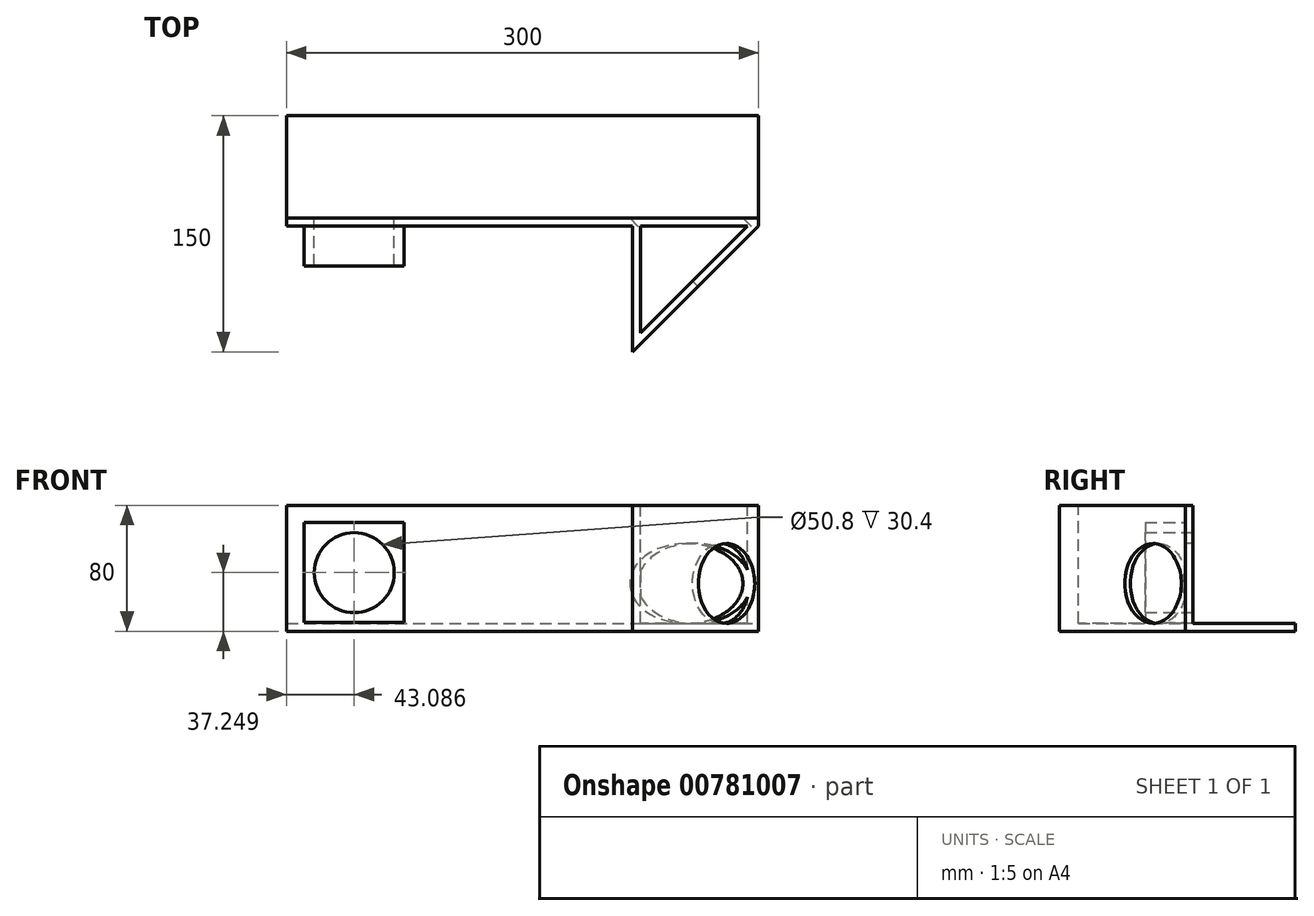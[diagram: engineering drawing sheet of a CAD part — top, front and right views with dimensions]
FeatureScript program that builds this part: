
annotation { "Feature Type Name" : "Feature", "Feature Type Description" : "" }
export const myFeature = defineFeature(function(context is Context, id is Id, definition is map)
    precondition{}
    {
        {
            var Q0;
            Q0=qCreatedBy(makeId("Top.planeOp"),FACE);
            var sketch = newSketch(context, id + "F0", { "sketchPlane" : qUnion([Q0])});
            skLineSegment(sketch, "E0.bottom", {"start": v(-205.2, 70) * mm, "end": v(94.8, 70) * mm});
            skLineSegment(sketch, "E0.top", {"start": v(-205.2, 0) * mm, "end": v(94.8, 0) * mm});
            skLineSegment(sketch, "E0.left", {"start": v(-205.2, 70) * mm, "end": v(-205.2, 0) * mm});
            skLineSegment(sketch, "E0.right", {"start": v(94.8, 70) * mm, "end": v(94.8, 0) * mm});
            skLineSegment(sketch, "E1", {"start": v(94.8, 0) * mm, "end": v(14.8, -80) * mm});
            skLineSegment(sketch, "E2", {"start": v(14.8, -80) * mm, "end": v(14.8, 0) * mm});
            skSolve(sketch);
        }
        {
            var Q0;
            Q0=makeQuery(id+"F0.imprint","IMPRINT",FACE,{"disambiguationData":[TD([[makeQuery(id+"F0.imprint","IMPRINT",EDGE,{"derivedFrom":sQuery(id+"F0.wireOp",EDGE,"E0.bottom")}),-1.0]])]});
            var Q1;
            {var subQ0=sQuery(id+"F0.wireOp",EDGE,"E1");Q1=makeQuery(id+"F0.imprint","IMPRINT",FACE,{"disambiguationData":[TD([[makeQuery(id+"F0.imprint","IMPRINT",EDGE,{"derivedFrom":subQ0}),-1.0]])]});}
            extrude(context, id + "F1", {"entities" : qUnion([Q0, Q1]), "depth" : 80 * mm, "offsetDistance" : 25.4 * mm});
        }
        {
            var Q0;
            Q0=makeQuery(id+"F1.opExtrude","CAP_FACE",FACE,{"disambiguationData":[OSD([sQuery(id+"F0.wireOp",EDGE,"E0.bottom"),sQuery(id+"F0.wireOp",EDGE,"E0.top"),sQuery(id+"F0.wireOp",EDGE,"E0.left"),sQuery(id+"F0.wireOp",EDGE,"E0.right"),sQuery(id+"F0.wireOp",EDGE,"E1"),sQuery(id+"F0.wireOp",EDGE,"E2")])],"isStart":false});
            var sketch = newSketch(context, id + "F2", { "sketchPlane" : qUnion([Q0])});
            skLineSegment(sketch, "E3", {"start": v(19.8, 0) * mm, "end": v(87.73, 0) * mm});
            skLineSegment(sketch, "E4", {"start": v(87.73, 0) * mm, "end": v(19.8, -67.93) * mm});
            skLineSegment(sketch, "E5", {"start": v(19.8, -67.93) * mm, "end": v(19.8, 0) * mm});
            skSolve(sketch);
        }
        {
            var Q0;
            Q0=makeQuery(id+"F2.imprint","IMPRINT",FACE,{"disambiguationData":[TD([[makeQuery(id+"F2.imprint","IMPRINT",EDGE,{"derivedFrom":sQuery(id+"F2.wireOp",EDGE,"E3")}),-1.0]])]});
            extrude(context, id + "F3", {"entities" : qUnion([Q0]), "operationType" : NewBodyOperationType.REMOVE, "oppositeDirection" : true, "depth" : 75 * mm, "offsetDistance" : 25.4 * mm});
        }
        {
            var Q0;
            Q0=makeQuery(id+"F1.opExtrude","SWEPT_FACE",FACE,{"disambiguationData":[OSD([sQuery(id+"F0.wireOp",EDGE,"E1")])]});
            var sketch = newSketch(context, id + "F4", { "sketchPlane" : qUnion([Q0])});
            skCircle(sketch, "E6", {"center": v(38.09, 30.4) * mm, "radius": 25.4 * mm});
            skSolve(sketch);
        }
        {
            var Q0;
            Q0=makeQuery(id+"F4.imprint","IMPRINT",FACE,{"disambiguationData":[TD([[makeQuery(id+"F4.imprint","IMPRINT",EDGE,{"derivedFrom":sQuery(id+"F4.wireOp",EDGE,"E6")}),1.0]])]});
            extrude(context, id + "F5", {"entities" : qUnion([Q0]), "operationType" : NewBodyOperationType.REMOVE, "oppositeDirection" : true, "depth" : 76.2 * mm, "offsetDistance" : 25.4 * mm});
        }
        {
            var Q0;
            Q0=makeQuery(id+"F1.opExtrude","SWEPT_FACE",FACE,{"disambiguationData":[OSD([sQuery(id+"F0.wireOp",EDGE,"E0.right")])]});
            var sketch = newSketch(context, id + "F6", { "sketchPlane" : qUnion([Q0])});
            skLineSegment(sketch, "E7", {"start": v(5, 80) * mm, "end": v(5, 5) * mm});
            skLineSegment(sketch, "E8", {"start": v(5, 5) * mm, "end": v(70, 5) * mm});
            skSolve(sketch);
        }
        {
            var Q0;
            Q0 = qSketchRegion(id + "F6", true);
            var Q1;
            {var subQ0=sQuery(id+"F6.wireOp",EDGE,"E7");Q1=makeQuery(id+"F6.imprint","IMPRINT",FACE,{"disambiguationData":[TD([[makeQuery(id+"F6.imprint","IMPRINT",EDGE,{"derivedFrom":subQ0}),1.0]])]});}
            extrude(context, id + "F7", {"entities" : qUnion([Q0, Q1]), "operationType" : NewBodyOperationType.REMOVE, "endBound" : BoundingType.THROUGH_ALL, "oppositeDirection" : true, "depth" : 25.4 * mm, "offsetDistance" : 25.4 * mm});
        }
        {
            var Q0;
            Q0=makeQuery(id+"F1.opExtrude","SWEPT_FACE",FACE,{"disambiguationData":[OSD([sQuery(id+"F0.wireOp",EDGE,"E0.top")])]});
            var sketch = newSketch(context, id + "F8", { "sketchPlane" : qUnion([Q0])});
            skLineSegment(sketch, "E9.bottom", {"start": v(-193.86, 69) * mm, "end": v(-130.36, 69) * mm});
            skLineSegment(sketch, "E9.top", {"start": v(-193.86, 5.5) * mm, "end": v(-130.36, 5.5) * mm});
            skLineSegment(sketch, "E9.left", {"start": v(-193.86, 69) * mm, "end": v(-193.86, 5.5) * mm});
            skLineSegment(sketch, "E9.right", {"start": v(-130.36, 69) * mm, "end": v(-130.36, 5.5) * mm});
            skCircle(sketch, "E10", {"center": v(-162.11, 37.25) * mm, "radius": 25.4 * mm});
            skPoint(sketch, "E11", {"position": v(-162.11, 69) * mm});
            skPoint(sketch, "E12", {"position": v(-130.36, 37.25) * mm});
            skPoint(sketch, "E13", {"position": v(-162.11, 5.5) * mm});
            skPoint(sketch, "E14", {"position": v(-193.86, 37.25) * mm});
            skSolve(sketch);
        }
        {
            var Q0;
            Q0=makeQuery(id+"F8.imprint","IMPRINT",FACE,{"disambiguationData":[TD([[makeQuery(id+"F8.imprint","IMPRINT",EDGE,{"derivedFrom":sQuery(id+"F8.wireOp",EDGE,"E9.bottom")}),-1.0]])]});
            extrude(context, id + "F9", {"entities" : qUnion([Q0]), "operationType" : NewBodyOperationType.ADD, "depth" : 25.4 * mm, "offsetDistance" : 25.4 * mm});
        }
        {
            var Q0;
            Q0=makeQuery(id+"F9.boolean.opBoolean","SPLIT",FACE,{"disambiguationData":[TD([makeQuery(id+"F9.opExtrude","SWEPT_FACE",FACE,{"disambiguationData":[OSD([sQuery(id+"F8.wireOp",EDGE,"E10")])]})])],"derivedFrom":makeQuery(id+"F1.opExtrude","SWEPT_FACE",FACE,{"disambiguationData":[OSD([sQuery(id+"F0.wireOp",EDGE,"E0.top")])]})});
            extrude(context, id + "F10", {"entities" : qUnion([Q0]), "operationType" : NewBodyOperationType.REMOVE, "endBound" : BoundingType.THROUGH_ALL, "oppositeDirection" : true, "depth" : 25.4 * mm, "offsetDistance" : 25.4 * mm});
        }
    });
